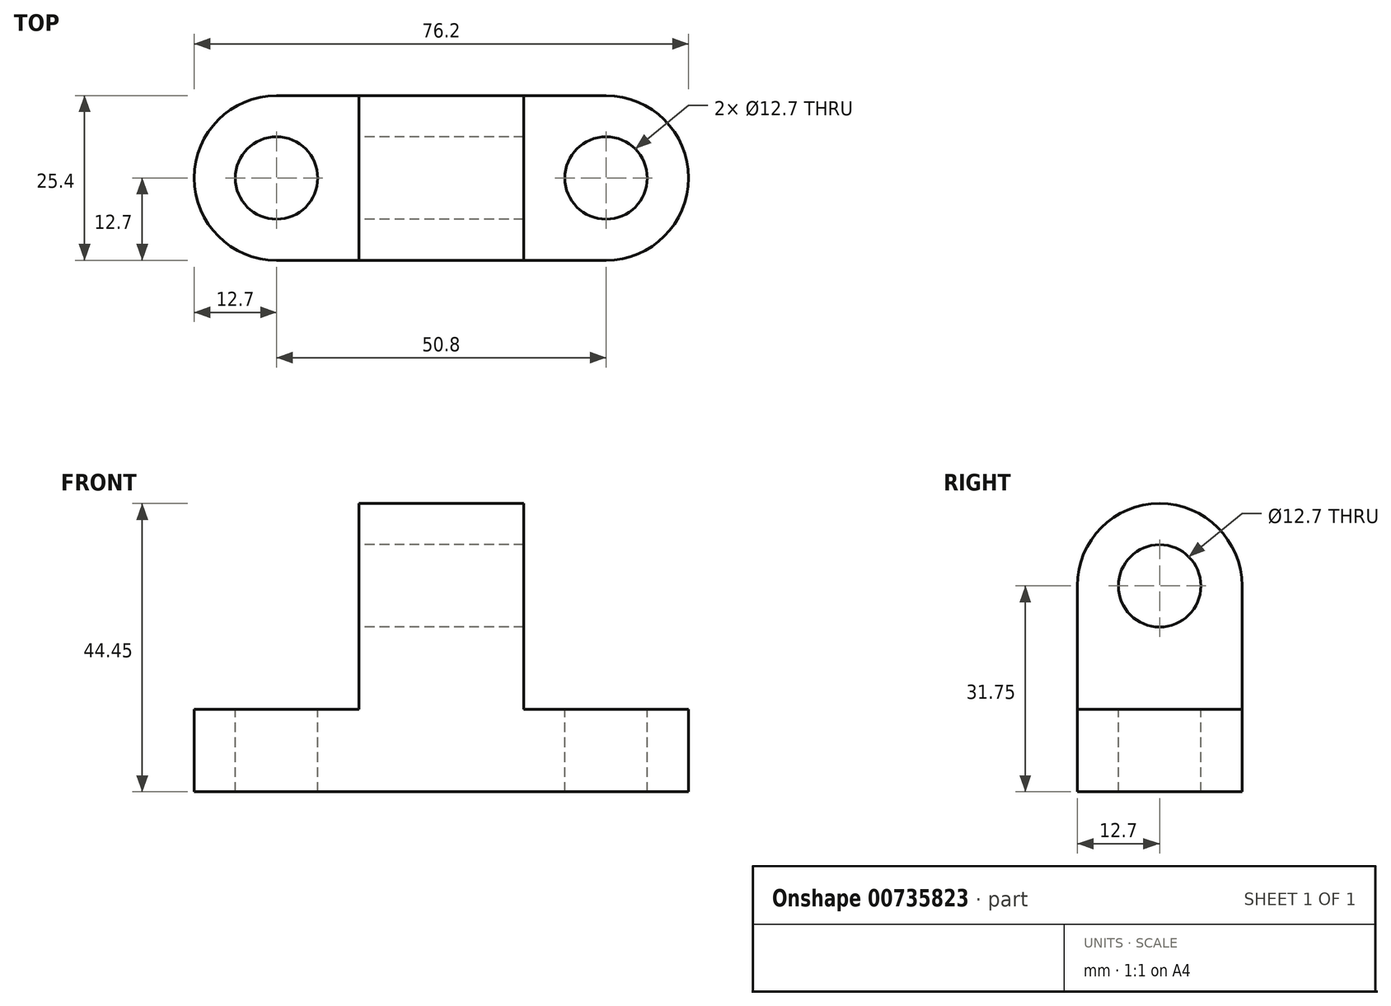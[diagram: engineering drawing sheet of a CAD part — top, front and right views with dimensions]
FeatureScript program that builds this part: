
annotation { "Feature Type Name" : "Feature", "Feature Type Description" : "" }
export const myFeature = defineFeature(function(context is Context, id is Id, definition is map)
    precondition{}
    {
        {
            var Q0;
            Q0=qCreatedBy(makeId("Top.planeOp"),FACE);
            var sketch = newSketch(context, id + "F0", { "sketchPlane" : qUnion([Q0])});
            skLineSegment(sketch, "E0", {"start": v(0, 0) * mm, "end": v(0, 25.4) * mm});
            skLineSegment(sketch, "E1", {"start": v(0, 25.4) * mm, "end": v(50.8, 25.4) * mm});
            skLineSegment(sketch, "E2", {"start": v(50.8, 25.4) * mm, "end": v(50.8, 0) * mm});
            skLineSegment(sketch, "E3", {"start": v(50.8, 0) * mm, "end": v(0, 0) * mm});
            skSolve(sketch);
        }
        {
            var Q0;
            Q0 = qSketchRegion(id + "F0", true);
            extrude(context, id + "F1", {"entities" : qUnion([Q0]), "depth" : 12.7 * mm, "offsetDistance" : 25.4 * mm});
        }
        {
            var Q0;
            Q0=makeQuery(id+"F1.opExtrude","CAP_FACE",FACE,{"disambiguationData":[OSD([sQuery(id+"F0.wireOp",EDGE,"E0"),sQuery(id+"F0.wireOp",EDGE,"E1"),sQuery(id+"F0.wireOp",EDGE,"E2"),sQuery(id+"F0.wireOp",EDGE,"E3")])],"isStart":false});
            var sketch = newSketch(context, id + "F2", { "sketchPlane" : qUnion([Q0])});
            skCircle(sketch, "E4", {"center": v(0, 12.7) * mm, "radius": 12.7 * mm});
            skSolve(sketch);
        }
        {
            var Q0;
            Q0 = qSketchRegion(id + "F2", true);
            extrude(context, id + "F3", {"entities" : qUnion([Q0]), "operationType" : NewBodyOperationType.ADD, "oppositeDirection" : true, "depth" : 12.7 * mm, "offsetDistance" : 25.4 * mm});
        }
        {
            var Q0;
            Q0=makeQuery(id+"F3.boolean.opBoolean","MERGE",FACE,{"derivedFrom":[makeQuery(id+"F1.opExtrude","CAP_FACE",FACE,{"disambiguationData":[OSD([sQuery(id+"F0.wireOp",EDGE,"E0"),sQuery(id+"F0.wireOp",EDGE,"E1"),sQuery(id+"F0.wireOp",EDGE,"E2"),sQuery(id+"F0.wireOp",EDGE,"E3")])],"isStart":false}),makeQuery(id+"F3.opExtrude","CAP_FACE",FACE,{"disambiguationData":[OSD([sQuery(id+"F2.wireOp",EDGE,"E4")])],"isStart":true})]});
            var sketch = newSketch(context, id + "F4", { "sketchPlane" : qUnion([Q0])});
            skCircle(sketch, "E5", {"center": v(50.8, 12.7) * mm, "radius": 12.7 * mm});
            skSolve(sketch);
        }
        {
            var Q0;
            Q0 = qSketchRegion(id + "F4", true);
            extrude(context, id + "F5", {"entities" : qUnion([Q0]), "operationType" : NewBodyOperationType.ADD, "oppositeDirection" : true, "depth" : 12.7 * mm, "offsetDistance" : 25.4 * mm});
        }
        {
            var Q0;
            Q0=makeQuery(id+"F5.boolean.opBoolean","MERGE",FACE,{"derivedFrom":[makeQuery(id+"F3.boolean.opBoolean","MERGE",FACE,{"derivedFrom":[makeQuery(id+"F1.opExtrude","CAP_FACE",FACE,{"disambiguationData":[OSD([sQuery(id+"F0.wireOp",EDGE,"E0"),sQuery(id+"F0.wireOp",EDGE,"E1"),sQuery(id+"F0.wireOp",EDGE,"E2"),sQuery(id+"F0.wireOp",EDGE,"E3")])],"isStart":false}),makeQuery(id+"F3.opExtrude","CAP_FACE",FACE,{"disambiguationData":[OSD([sQuery(id+"F2.wireOp",EDGE,"E4")])],"isStart":true})]}),makeQuery(id+"F5.opExtrude","CAP_FACE",FACE,{"disambiguationData":[OSD([sQuery(id+"F4.wireOp",EDGE,"E5")])],"isStart":true})]});
            var sketch = newSketch(context, id + "F6", { "sketchPlane" : qUnion([Q0])});
            skLineSegment(sketch, "E6", {"start": v(12.7, 0) * mm, "end": v(12.7, 25.4) * mm});
            skLineSegment(sketch, "E7", {"start": v(12.7, 25.4) * mm, "end": v(38.1, 25.4) * mm});
            skLineSegment(sketch, "E8", {"start": v(38.1, 25.4) * mm, "end": v(38.1, 0) * mm});
            skLineSegment(sketch, "E9", {"start": v(38.1, 0) * mm, "end": v(12.7, 0) * mm});
            skSolve(sketch);
        }
        {
            var Q0;
            Q0 = qSketchRegion(id + "F6", true);
            extrude(context, id + "F7", {"entities" : qUnion([Q0]), "operationType" : NewBodyOperationType.ADD, "depth" : 19.05 * mm, "offsetDistance" : 25.4 * mm});
        }
        {
            var Q0;
            Q0=makeQuery(id+"F7.opExtrude","SWEPT_FACE",FACE,{"disambiguationData":[OSD([sQuery(id+"F6.wireOp",EDGE,"E6")])]});
            var sketch = newSketch(context, id + "F8", { "sketchPlane" : qUnion([Q0])});
            skCircle(sketch, "E10", {"center": v(-12.7, 31.75) * mm, "radius": 12.7 * mm});
            skSolve(sketch);
        }
        {
            var Q0;
            Q0 = qSketchRegion(id + "F8", true);
            extrude(context, id + "F9", {"entities" : qUnion([Q0]), "operationType" : NewBodyOperationType.ADD, "oppositeDirection" : true, "depth" : 25.4 * mm, "offsetDistance" : 25.4 * mm});
        }
        {
            var Q0;
            Q0=makeQuery(id+"F9.boolean.opBoolean","MERGE",FACE,{"derivedFrom":[makeQuery(id+"F7.opExtrude","SWEPT_FACE",FACE,{"disambiguationData":[OSD([sQuery(id+"F6.wireOp",EDGE,"E6")])]}),makeQuery(id+"F9.opExtrude","CAP_FACE",FACE,{"disambiguationData":[OSD([sQuery(id+"F8.wireOp",EDGE,"E10")])],"isStart":true})]});
            var sketch = newSketch(context, id + "F10", { "sketchPlane" : qUnion([Q0])});
            skCircle(sketch, "E11", {"center": v(-12.7, 31.75) * mm, "radius": 6.35 * mm});
            skSolve(sketch);
        }
        {
            var Q0;
            Q0 = qSketchRegion(id + "F10", true);
            extrude(context, id + "F11", {"entities" : qUnion([Q0]), "operationType" : NewBodyOperationType.REMOVE, "oppositeDirection" : true, "depth" : 25.4 * mm, "offsetDistance" : 25.4 * mm});
        }
        {
            var Q0;
            {var subQ0=sQuery(id+"F4.wireOp",EDGE,"E5");var subQ1=sQuery(id+"F0.wireOp",EDGE,"E3");var subQ2=sQuery(id+"F0.wireOp",EDGE,"E1");Q0=makeQuery(id+"F7.boolean.opBoolean","SPLIT",FACE,{"disambiguationData":[TD([makeQuery(id+"F5.opExtrude","SWEPT_FACE",FACE,{"disambiguationData":[OSD([subQ0])]})])],"derivedFrom":makeQuery(id+"F5.boolean.opBoolean","MERGE",FACE,{"derivedFrom":[makeQuery(id+"F3.boolean.opBoolean","MERGE",FACE,{"derivedFrom":[makeQuery(id+"F1.opExtrude","CAP_FACE",FACE,{"disambiguationData":[OSD([sQuery(id+"F0.wireOp",EDGE,"E0"),subQ2,sQuery(id+"F0.wireOp",EDGE,"E2"),subQ1])],"isStart":false}),makeQuery(id+"F3.opExtrude","CAP_FACE",FACE,{"disambiguationData":[OSD([sQuery(id+"F2.wireOp",EDGE,"E4")])],"isStart":true})]}),makeQuery(id+"F5.opExtrude","CAP_FACE",FACE,{"disambiguationData":[OSD([subQ0])],"isStart":true})]})});}
            var sketch = newSketch(context, id + "F12", { "sketchPlane" : qUnion([Q0])});
            skCircle(sketch, "E12", {"center": v(50.8, 12.7) * mm, "radius": 6.35 * mm});
            skCircle(sketch, "E13", {"center": v(0, 12.7) * mm, "radius": 6.35 * mm});
            skSolve(sketch);
        }
        {
            var Q0;
            Q0 = qSketchRegion(id + "F12", true);
            extrude(context, id + "F13", {"entities" : qUnion([Q0]), "operationType" : NewBodyOperationType.REMOVE, "oppositeDirection" : true, "depth" : 12.7 * mm, "offsetDistance" : 25.4 * mm});
        }
    });
